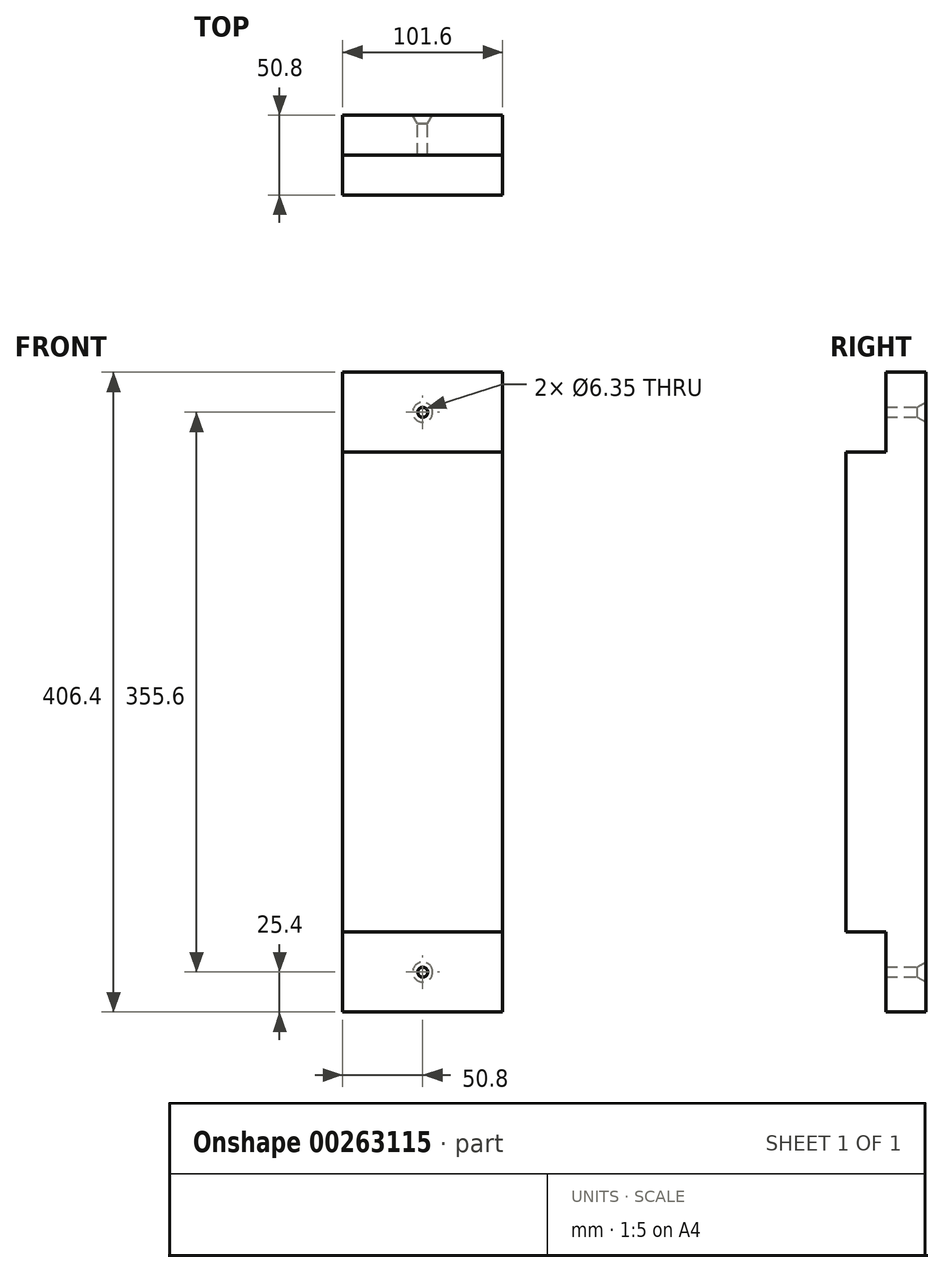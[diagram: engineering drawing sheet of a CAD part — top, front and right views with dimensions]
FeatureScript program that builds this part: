
annotation { "Feature Type Name" : "Feature", "Feature Type Description" : "" }
export const myFeature = defineFeature(function(context is Context, id is Id, definition is map)
    precondition{}
    {
        {
            var Q0;
            Q0=qCreatedBy(makeId("Top.planeOp"),FACE);
            var sketch = newSketch(context, id + "F0", { "sketchPlane" : qUnion([Q0])});
            skLineSegment(sketch, "E0.bottom", {"start": v(50.8, 25.4) * mm, "end": v(-50.8, 25.4) * mm});
            skLineSegment(sketch, "E0.top", {"start": v(50.8, -25.4) * mm, "end": v(-50.8, -25.4) * mm});
            skLineSegment(sketch, "E0.left", {"start": v(50.8, 25.4) * mm, "end": v(50.8, -25.4) * mm});
            skLineSegment(sketch, "E0.right", {"start": v(-50.8, 25.4) * mm, "end": v(-50.8, -25.4) * mm});
            skPoint(sketch, "E0.middle", {"position": v(0, 0) * mm});
            skSolve(sketch);
        }
        {
            var Q0;
            Q0=qSketchRegion(id+"F0",true);
            extrude(context, id + "F1", {"entities" : qUnion([Q0]), "depth" : 406.4 * mm});
        }
        {
            var Q0;
            Q0=makeQuery(id+"F1.opExtrude","CAP_FACE",FACE,{"disambiguationData":[OSD([sQuery(id+"F0.wireOp",EDGE,"E0.bottom"),sQuery(id+"F0.wireOp",EDGE,"E0.top"),sQuery(id+"F0.wireOp",EDGE,"E0.left"),sQuery(id+"F0.wireOp",EDGE,"E0.right")])],"isStart":false});
            var sketch = newSketch(context, id + "F2", { "sketchPlane" : qUnion([Q0])});
            skLineSegment(sketch, "E1.bottom", {"start": v(-50.8, -25.4) * mm, "end": v(50.8, -25.4) * mm});
            skLineSegment(sketch, "E1.top", {"start": v(-50.8, 0) * mm, "end": v(50.8, 0) * mm});
            skLineSegment(sketch, "E1.left", {"start": v(-50.8, -25.4) * mm, "end": v(-50.8, 0) * mm});
            skLineSegment(sketch, "E1.right", {"start": v(50.8, -25.4) * mm, "end": v(50.8, 0) * mm});
            skSolve(sketch);
        }
        {
            var Q0;
            Q0 = qSketchRegion(id + "F2", true);
            extrude(context, id + "F3", {"entities" : qUnion([Q0]), "operationType" : NewBodyOperationType.REMOVE, "oppositeDirection" : true, "depth" : 50.8 * mm});
        }
        {
            var Q0;
            Q0=makeQuery(id+"F1.opExtrude","CAP_FACE",FACE,{"disambiguationData":[OSD([sQuery(id+"F0.wireOp",EDGE,"E0.bottom"),sQuery(id+"F0.wireOp",EDGE,"E0.top"),sQuery(id+"F0.wireOp",EDGE,"E0.left"),sQuery(id+"F0.wireOp",EDGE,"E0.right")])],"isStart":true});
            var sketch = newSketch(context, id + "F4", { "sketchPlane" : qUnion([Q0])});
            skLineSegment(sketch, "E2.bottom", {"start": v(-50.8, 25.4) * mm, "end": v(50.8, 25.4) * mm});
            skLineSegment(sketch, "E2.top", {"start": v(-50.8, 0) * mm, "end": v(50.8, 0) * mm});
            skLineSegment(sketch, "E2.left", {"start": v(-50.8, 25.4) * mm, "end": v(-50.8, 0) * mm});
            skLineSegment(sketch, "E2.right", {"start": v(50.8, 25.4) * mm, "end": v(50.8, 0) * mm});
            skSolve(sketch);
        }
        {
            var Q0;
            Q0 = qSketchRegion(id + "F4", true);
            extrude(context, id + "F5", {"entities" : qUnion([Q0]), "operationType" : NewBodyOperationType.REMOVE, "oppositeDirection" : true, "depth" : 50.8 * mm});
        }
        {
            var Q0;
            Q0=makeQuery(id+"F1.opExtrude","SWEPT_FACE",FACE,{"disambiguationData":[OSD([sQuery(id+"F0.wireOp",EDGE,"E0.bottom")])]});
            var sketch = newSketch(context, id + "F6", { "sketchPlane" : qUnion([Q0])});
            skCircle(sketch, "E3", {"center": v(0, 381) * mm, "radius": 3.17 * mm});
            skPoint(sketch, "E3.centerSnap0", {"position": v(0, 406.4) * mm});
            skCircle(sketch, "E4", {"center": v(0, 25.4) * mm, "radius": 3.18 * mm});
            skSolve(sketch);
        }
        {
            var Q0;
            Q0 = qSketchRegion(id + "F6", true);
            extrude(context, id + "F7", {"entities" : qUnion([Q0]), "operationType" : NewBodyOperationType.REMOVE, "endBound" : BoundingType.THROUGH_ALL, "oppositeDirection" : true, "depth" : 25.4 * mm});
        }
        {
            var Q0;
            Q0=makeQuery(id+"F1.opExtrude","SWEPT_FACE",FACE,{"disambiguationData":[OSD([sQuery(id+"F0.wireOp",EDGE,"E0.bottom")])]});
            var sketch = newSketch(context, id + "F8", { "sketchPlane" : qUnion([Q0])});
            skCircle(sketch, "E5", {"center": v(0, 381) * mm, "radius": 6.35 * mm});
            skCircle(sketch, "E6", {"center": v(0, 25.4) * mm, "radius": 6.35 * mm});
            skSolve(sketch);
        }
        {
            var Q0;
            Q0 = qSketchRegion(id + "F8", true);
            extrude(context, id + "F9", {"entities" : qUnion([Q0]), "operationType" : NewBodyOperationType.REMOVE, "oppositeDirection" : true, "depth" : 6.35 * mm, "hasDraft" : true, "draftAngle" : 30 * degree, "draftPullDirection" : true});
        }
    });
